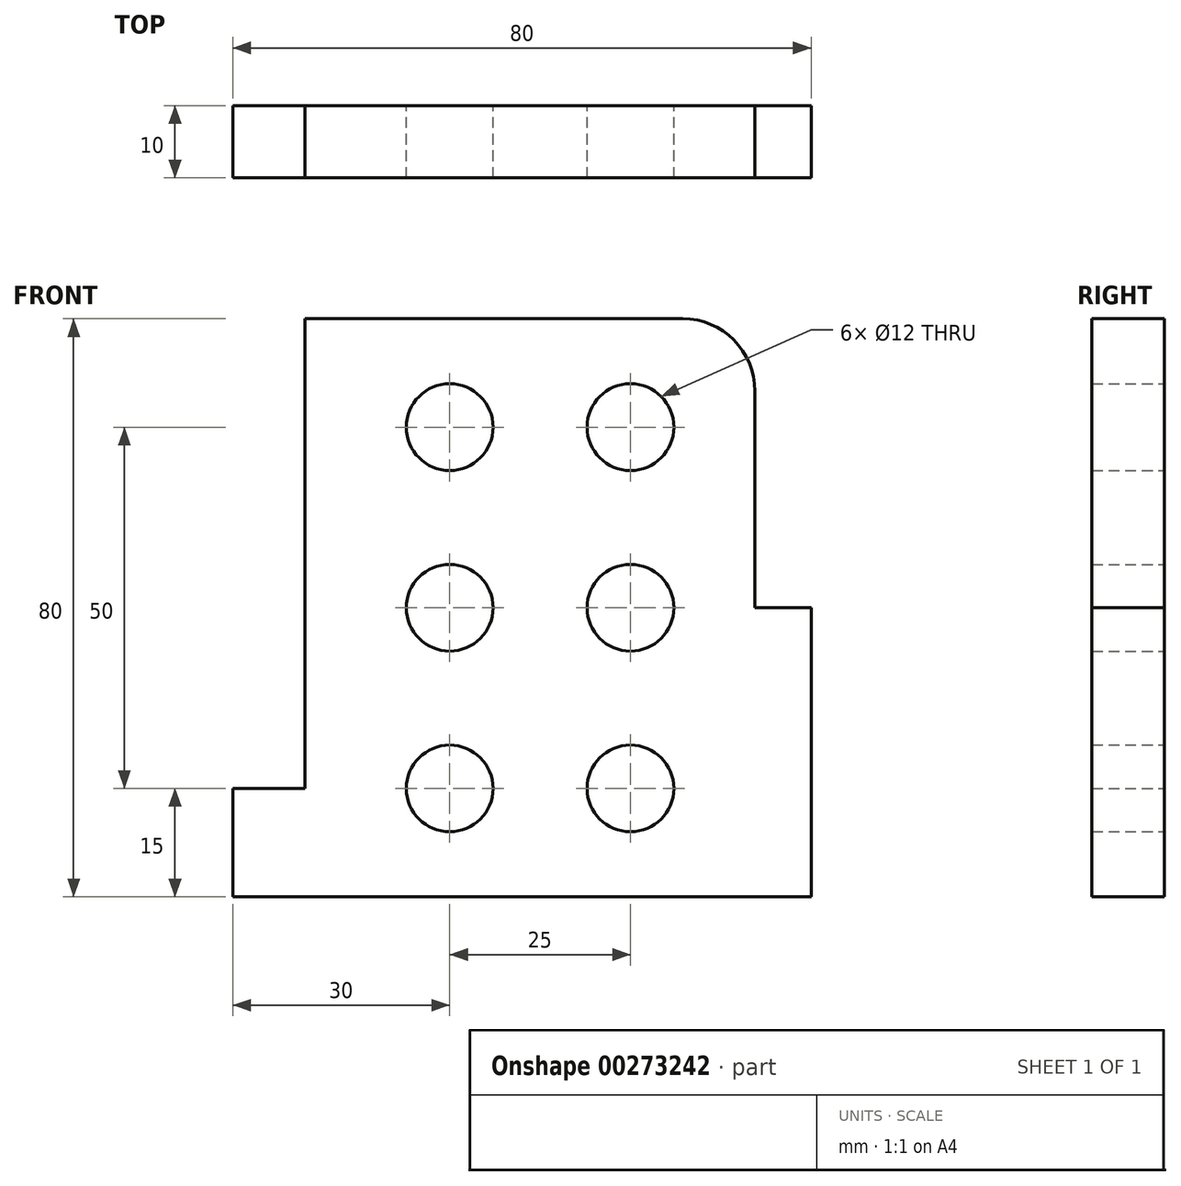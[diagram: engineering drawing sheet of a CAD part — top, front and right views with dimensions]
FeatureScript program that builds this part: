
annotation { "Feature Type Name" : "Feature", "Feature Type Description" : "" }
export const myFeature = defineFeature(function(context is Context, id is Id, definition is map)
    precondition{}
    {
        {
            var Q0;
            Q0=qCreatedBy(makeId("Front.planeOp"),FACE);
            var sketch = newSketch(context, id + "F0", { "sketchPlane" : qUnion([Q0])});
            skLineSegment(sketch, "E0", {"start": v(0, 0) * mm, "end": v(80, 0) * mm});
            skLineSegment(sketch, "E1", {"start": v(80, 0) * mm, "end": v(80, 40) * mm});
            skLineSegment(sketch, "E2", {"start": v(0, 0) * mm, "end": v(0, 15) * mm});
            skLineSegment(sketch, "E3", {"start": v(0, 15) * mm, "end": v(10, 15) * mm});
            skLineSegment(sketch, "E4", {"start": v(10, 15) * mm, "end": v(10, 80) * mm});
            skLineSegment(sketch, "E5", {"start": v(80, 40) * mm, "end": v(72.22, 40) * mm});
            skLineSegment(sketch, "E6", {"start": v(10, 80) * mm, "end": v(62.22, 80) * mm});
            skLineSegment(sketch, "E7", {"start": v(72.22, 70) * mm, "end": v(72.22, 40) * mm});
            skPoint(sketch, "E8.visualSharp", {"position": v(72.22, 80) * mm});
            skArc(sketch, "E8.filletArc", {"start": v(72.22, 70) * mm, "mid": v(69.3, 77.07) * mm, "end": v(62.22, 80) * mm});
            skCircle(sketch, "E9", {"center": v(30, 15) * mm, "radius": 6 * mm});
            skCircle(sketch, "E10", {"center": v(30, 40) * mm, "radius": 6 * mm});
            skCircle(sketch, "E11", {"center": v(30, 65) * mm, "radius": 6 * mm});
            skCircle(sketch, "E12", {"center": v(55, 15) * mm, "radius": 6 * mm});
            skCircle(sketch, "E13", {"center": v(55, 40) * mm, "radius": 6 * mm});
            skCircle(sketch, "E14", {"center": v(55, 65) * mm, "radius": 6 * mm});
            skSolve(sketch);
        }
        {
            var Q0;
            Q0 = qSketchRegion(id + "F0", true);
            extrude(context, id + "F1", {"entities" : qUnion([Q0]), "depth" : 10 * mm});
        }
    });
